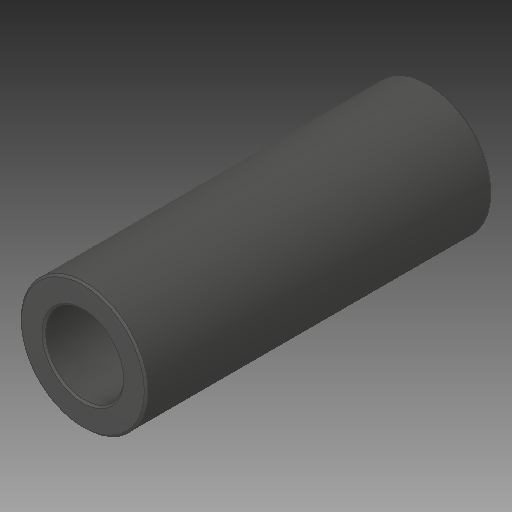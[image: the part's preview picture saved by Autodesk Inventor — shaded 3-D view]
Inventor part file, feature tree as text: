
AUTODESK INVENTOR PART (.ipt)
format: ipt  version: 2019 (Build 230136000, 136)  size: 106,496 bytes
history: native  units: in
note: dims shown in document units (in); Inventor stores cm internally (conversion verified against a paired STEP export)
features: chamfer x1
ambient origin geometry x8: Origin, YZ Plane, XZ Plane, XY Plane, X Axis, Y Axis, Z Axis, Center Point
bodies: Solid1 (feature_tree)
feature tree (1):
  chamfer  "Chamfer1"  [1 undecoded]
note: 1 required parameter value undecoded (feature->parameter linkage not recoverable at this tier; creation-order binding heuristic only, values carry confidence <= 0.55)
